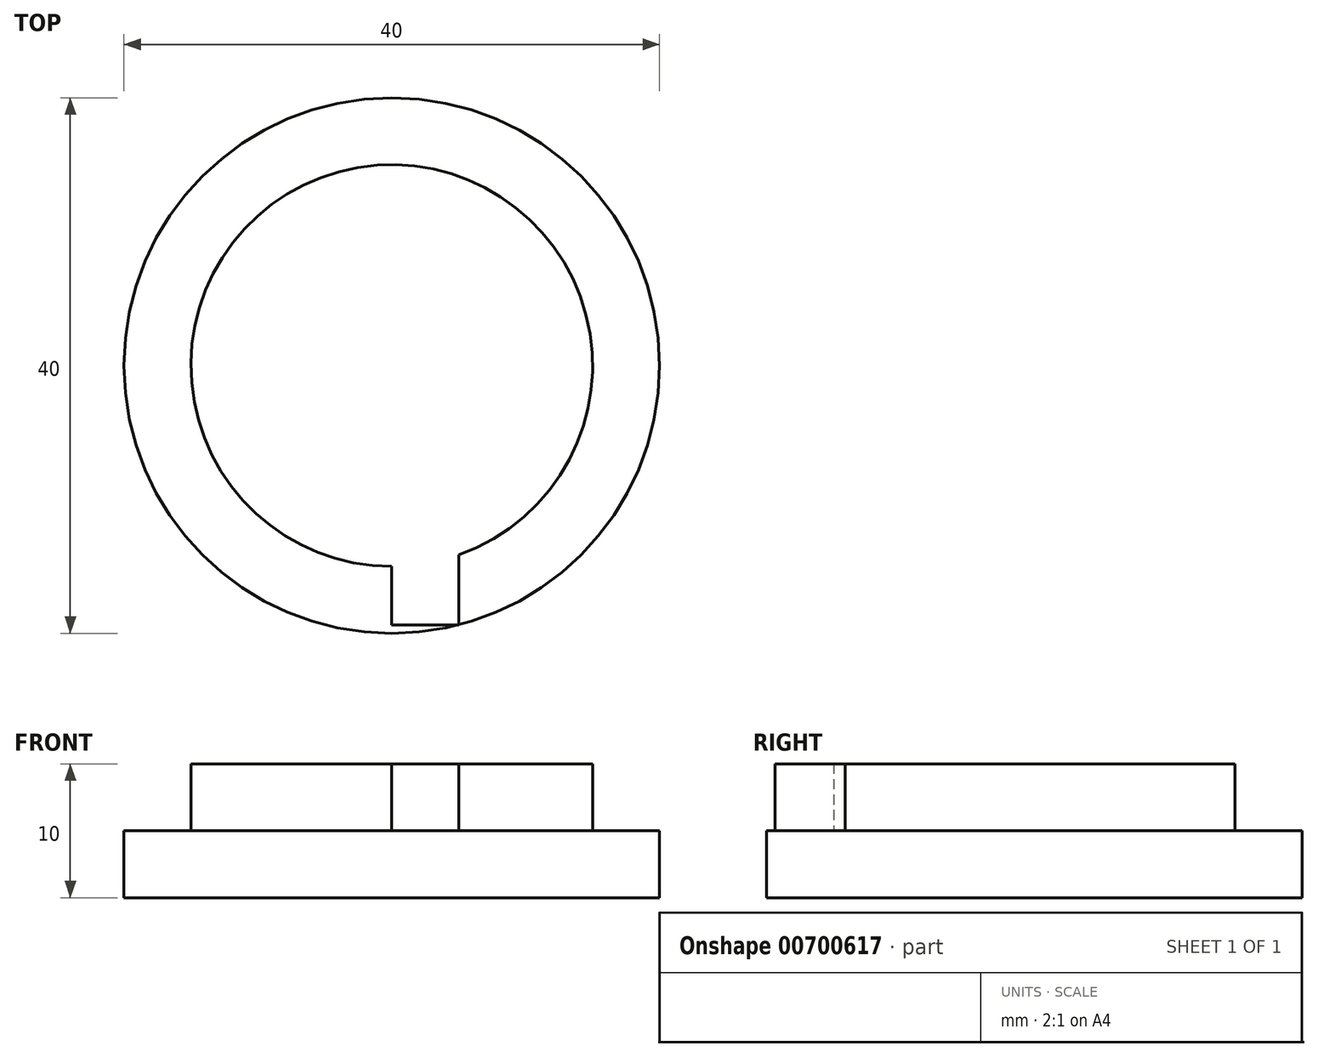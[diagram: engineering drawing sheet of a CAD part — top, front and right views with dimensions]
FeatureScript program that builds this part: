
annotation { "Feature Type Name" : "Feature", "Feature Type Description" : "" }
export const myFeature = defineFeature(function(context is Context, id is Id, definition is map)
    precondition{}
    {
        {
            var Q0;
            Q0=qCreatedBy(makeId("Top.planeOp"),FACE);
            var sketch = newSketch(context, id + "F0", { "sketchPlane" : qUnion([Q0])});
            skCircle(sketch, "E0", {"center": v(0, 0) * mm, "radius": 20 * mm});
            skSolve(sketch);
        }
        {
            var Q0;
            Q0 = qSketchRegion(id + "F0", true);
            extrude(context, id + "F1", {"entities" : qUnion([Q0]), "depth" : 5 * mm, "offsetDistance" : 25 * mm});
        }
        {
            var Q0;
            Q0=makeQuery(id+"F1.opExtrude","CAP_FACE",FACE,{"disambiguationData":[OSD([sQuery(id+"F0.wireOp",EDGE,"E0")])],"isStart":false});
            var sketch = newSketch(context, id + "F2", { "sketchPlane" : qUnion([Q0])});
            skCircle(sketch, "E1", {"center": v(0, 0) * mm, "radius": 15 * mm});
            skSolve(sketch);
        }
        {
            var Q0;
            Q0 = qSketchRegion(id + "F2", true);
            extrude(context, id + "F3", {"entities" : qUnion([Q0]), "operationType" : NewBodyOperationType.ADD, "depth" : 5 * mm, "offsetDistance" : 25 * mm});
        }
        {
            var Q0;
            Q0=makeQuery(id+"F1.opExtrude","CAP_FACE",FACE,{"disambiguationData":[OSD([sQuery(id+"F0.wireOp",EDGE,"E0")])],"isStart":false});
            var sketch = newSketch(context, id + "F4", { "sketchPlane" : qUnion([Q0])});
            skLineSegment(sketch, "E2.bottom", {"start": v(5, -19.36) * mm, "end": v(0, -19.36) * mm});
            skLineSegment(sketch, "E2.top", {"start": v(5, 0) * mm, "end": v(0, 0) * mm});
            skLineSegment(sketch, "E2.left", {"start": v(5, -19.36) * mm, "end": v(5, 0) * mm});
            skLineSegment(sketch, "E2.right", {"start": v(0, -19.36) * mm, "end": v(0, 0) * mm});
            skSolve(sketch);
        }
        {
            var Q0;
            {var subQ0=sQuery(id+"F4.wireOp",EDGE,"E2.bottom");Q0=makeQuery(id+"F4.imprint","IMPRINT",FACE,{"disambiguationData":[TD([[makeQuery(id+"F4.imprint","IMPRINT",EDGE,{"derivedFrom":subQ0}),-1.0]])]});}
            extrude(context, id + "F5", {"entities" : qUnion([Q0]), "operationType" : NewBodyOperationType.ADD, "depth" : 5 * mm, "offsetDistance" : 25 * mm});
        }
    });
